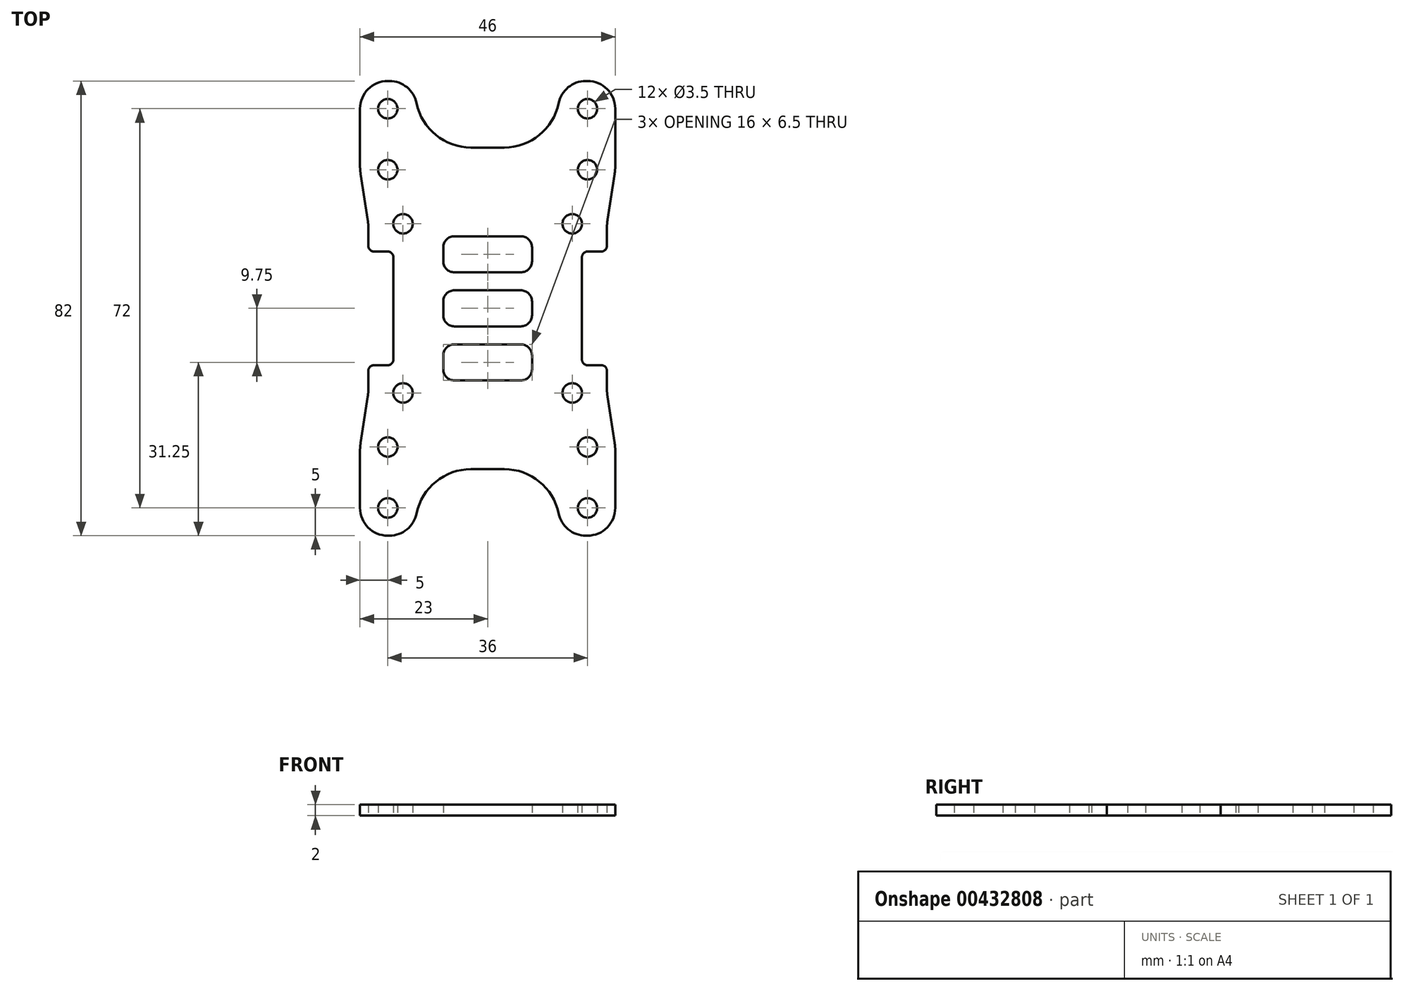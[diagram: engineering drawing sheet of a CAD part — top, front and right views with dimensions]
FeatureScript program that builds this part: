
annotation { "Feature Type Name" : "Feature", "Feature Type Description" : "" }
export const myFeature = defineFeature(function(context is Context, id is Id, definition is map)
    precondition{}
    {
        {
            var Q0;
            Q0=qCreatedBy(makeId("Top.planeOp"),FACE);
            var sketch = newSketch(context, id + "F0", { "sketchPlane" : qUnion([Q0])});
            skCircle(sketch, "E0", {"center": v(-18, 36) * mm, "radius": 1.75 * mm});
            skCircle(sketch, "E1", {"center": v(-18, 25) * mm, "radius": 1.75 * mm});
            skCircle(sketch, "E2", {"center": v(-15.25, 15.25) * mm, "radius": 1.75 * mm});
            skLineSegment(sketch, "E3", {"start": v(-18, 41) * mm, "end": v(-13, 41) * mm});
            skLineSegment(sketch, "E4", {"start": v(-23, 36) * mm, "end": v(-23, 25.76) * mm});
            skLineSegment(sketch, "E5", {"start": v(-21.5, 14.49) * mm, "end": v(-21.5, 11.25) * mm});
            skLineSegment(sketch, "E6", {"start": v(-22.88, 24.24) * mm, "end": v(-21.62, 16) * mm});
            skPoint(sketch, "E7.visualSharp", {"position": v(-23, 25) * mm});
            skArc(sketch, "E7.filletArc", {"start": v(-23, 25.76) * mm, "mid": v(-22.97, 25) * mm, "end": v(-22.88, 24.24) * mm});
            skPoint(sketch, "E8.visualSharp", {"position": v(-21.5, 15.25) * mm});
            skArc(sketch, "E8.filletArc", {"start": v(-21.5, 14.49) * mm, "mid": v(-21.53, 15.25) * mm, "end": v(-21.62, 16) * mm});
            skPoint(sketch, "E9.visualSharp", {"position": v(-23, 41) * mm});
            skArc(sketch, "E9.filletArc", {"start": v(-18, 41) * mm, "mid": v(-21.54, 39.54) * mm, "end": v(-23, 36) * mm});
            skArc(sketch, "E10.MirrorCS", {"start": v(23, 25.76) * mm, "mid": v(22.97, 25) * mm, "end": v(22.88, 24.24) * mm});
            skArc(sketch, "E11.MirrorCS", {"start": v(21.5, 14.49) * mm, "mid": v(21.53, 15.25) * mm, "end": v(21.62, 16) * mm});
            skCircle(sketch, "E12.MirrorC", {"center": v(18, 36) * mm, "radius": 1.75 * mm});
            skLineSegment(sketch, "E13.MirrorCS", {"start": v(21.5, 14.49) * mm, "end": v(21.5, 11.25) * mm});
            skLineSegment(sketch, "E14.MirrorCS", {"start": v(22.88, 24.24) * mm, "end": v(21.62, 16) * mm});
            skPoint(sketch, "E15.MirrorP", {"position": v(23, 25) * mm});
            skLineSegment(sketch, "E16.MirrorCS", {"start": v(23, 36) * mm, "end": v(23, 25.76) * mm});
            skLineSegment(sketch, "E17.MirrorCS", {"start": v(18, 41) * mm, "end": v(13, 41) * mm});
            skArc(sketch, "E18.MirrorCS", {"start": v(18, 41) * mm, "mid": v(21.54, 39.54) * mm, "end": v(23, 36) * mm});
            skPoint(sketch, "E19.MirrorP", {"position": v(21.5, 15.25) * mm});
            skCircle(sketch, "E20.MirrorC", {"center": v(15.25, 15.25) * mm, "radius": 1.75 * mm});
            skCircle(sketch, "E21.MirrorC", {"center": v(18, 25) * mm, "radius": 1.75 * mm});
            skPoint(sketch, "E22.MirrorP", {"position": v(23, 41) * mm});
            skArc(sketch, "E23.MirrorCS", {"start": v(-23, -25.76) * mm, "mid": v(-22.97, -25) * mm, "end": v(-22.88, -24.24) * mm});
            skArc(sketch, "E24.MirrorCS", {"start": v(-21.5, -14.49) * mm, "mid": v(-21.53, -15.25) * mm, "end": v(-21.62, -16) * mm});
            skArc(sketch, "E25.MirrorCS", {"start": v(23, -25.76) * mm, "mid": v(22.97, -25) * mm, "end": v(22.88, -24.24) * mm});
            skArc(sketch, "E26.MirrorCS", {"start": v(21.5, -14.49) * mm, "mid": v(21.53, -15.25) * mm, "end": v(21.62, -16) * mm});
            skCircle(sketch, "E27.MirrorC", {"center": v(-18, -36) * mm, "radius": 1.75 * mm});
            skLineSegment(sketch, "E28.MirrorCS", {"start": v(21.5, -14.49) * mm, "end": v(21.5, -11.25) * mm});
            skPoint(sketch, "E29.MirrorP", {"position": v(21.5, -15.25) * mm});
            skCircle(sketch, "E30.MirrorC", {"center": v(18, -25) * mm, "radius": 1.75 * mm});
            skArc(sketch, "E31.MirrorCS", {"start": v(18, -41) * mm, "mid": v(21.54, -39.54) * mm, "end": v(23, -36) * mm});
            skPoint(sketch, "E32.MirrorP", {"position": v(23, -25) * mm});
            skPoint(sketch, "E33.MirrorP", {"position": v(-21.5, -15.25) * mm});
            skCircle(sketch, "E34.MirrorC", {"center": v(-15.25, -15.25) * mm, "radius": 1.75 * mm});
            skLineSegment(sketch, "E35.MirrorCS", {"start": v(22.88, -24.24) * mm, "end": v(21.62, -16) * mm});
            skLineSegment(sketch, "E36.MirrorCS", {"start": v(23, -36) * mm, "end": v(23, -25.76) * mm});
            skPoint(sketch, "E37.MirrorP", {"position": v(-23, -41) * mm});
            skPoint(sketch, "E38.MirrorP", {"position": v(-23, -25) * mm});
            skPoint(sketch, "E39.MirrorP", {"position": v(23, -41) * mm});
            skLineSegment(sketch, "E40.MirrorCS", {"start": v(-18, -41) * mm, "end": v(-13, -41) * mm});
            skCircle(sketch, "E41.MirrorC", {"center": v(-18, -25) * mm, "radius": 1.75 * mm});
            skLineSegment(sketch, "E42.MirrorCS", {"start": v(-23, -36) * mm, "end": v(-23, -25.76) * mm});
            skLineSegment(sketch, "E43.MirrorCS", {"start": v(-21.5, -14.49) * mm, "end": v(-21.5, -11.25) * mm});
            skLineSegment(sketch, "E44.MirrorCS", {"start": v(-22.88, -24.24) * mm, "end": v(-21.62, -16) * mm});
            skArc(sketch, "E45.MirrorCS", {"start": v(-18, -41) * mm, "mid": v(-21.54, -39.54) * mm, "end": v(-23, -36) * mm});
            skCircle(sketch, "E46.MirrorC", {"center": v(18, -36) * mm, "radius": 1.75 * mm});
            skCircle(sketch, "E47.MirrorC", {"center": v(15.25, -15.25) * mm, "radius": 1.75 * mm});
            skLineSegment(sketch, "E48.MirrorCS", {"start": v(18, -41) * mm, "end": v(13, -41) * mm});
            skLineSegment(sketch, "E49", {"start": v(-13, 41) * mm, "end": v(-13, 39) * mm});
            skLineSegment(sketch, "E50", {"start": v(-3, 29) * mm, "end": v(0, 29) * mm});
            skPoint(sketch, "E51.visualSharp", {"position": v(-13, 29) * mm});
            skArc(sketch, "E51.filletArc", {"start": v(-13, 39) * mm, "mid": v(-10.07, 31.93) * mm, "end": v(-3, 29) * mm});
            skArc(sketch, "E52.MirrorCS", {"start": v(13, 39) * mm, "mid": v(10.07, 31.93) * mm, "end": v(3, 29) * mm});
            skLineSegment(sketch, "E53.MirrorCS", {"start": v(13, 41) * mm, "end": v(13, 39) * mm});
            skLineSegment(sketch, "E54.MirrorCS", {"start": v(3, 29) * mm, "end": v(0, 29) * mm});
            skLineSegment(sketch, "E55.MirrorCS", {"start": v(-13, -41) * mm, "end": v(-13, -39) * mm});
            skArc(sketch, "E56.MirrorCS", {"start": v(-13, -39) * mm, "mid": v(-10.07, -31.93) * mm, "end": v(-3, -29) * mm});
            skLineSegment(sketch, "E57.MirrorCS", {"start": v(-3, -29) * mm, "end": v(0, -29) * mm});
            skLineSegment(sketch, "E58.MirrorCS", {"start": v(3, -29) * mm, "end": v(0, -29) * mm});
            skArc(sketch, "E59.MirrorCS", {"start": v(13, -39) * mm, "mid": v(10.07, -31.93) * mm, "end": v(3, -29) * mm});
            skLineSegment(sketch, "E60.MirrorCS", {"start": v(13, -41) * mm, "end": v(13, -39) * mm});
            skPoint(sketch, "E61.orphan", {"position": v(0, 41) * mm});
            skPoint(sketch, "E62.orphan", {"position": v(0, -41) * mm});
            skLineSegment(sketch, "E63", {"start": v(-17, 9.25) * mm, "end": v(-17, -9.25) * mm});
            skLineSegment(sketch, "E64", {"start": v(-18, 10.25) * mm, "end": v(-20.5, 10.25) * mm});
            skLineSegment(sketch, "E65", {"start": v(-18, -10.25) * mm, "end": v(-20.5, -10.25) * mm});
            skPoint(sketch, "E66.orphan", {"position": v(-21.5, 0) * mm});
            skPoint(sketch, "E67.visualSharp", {"position": v(-17, 10.25) * mm});
            skArc(sketch, "E67.filletArc", {"start": v(-17, 9.25) * mm, "mid": v(-17.3, 9.96) * mm, "end": v(-18, 10.25) * mm});
            skPoint(sketch, "E68.visualSharp", {"position": v(-17, -10.25) * mm});
            skArc(sketch, "E68.filletArc", {"start": v(-18, -10.25) * mm, "mid": v(-17.3, -9.96) * mm, "end": v(-17, -9.25) * mm});
            skPoint(sketch, "E69.visualSharp", {"position": v(-21.5, 10.25) * mm});
            skArc(sketch, "E69.filletArc", {"start": v(-21.5, 11.25) * mm, "mid": v(-21.2, 10.54) * mm, "end": v(-20.5, 10.25) * mm});
            skPoint(sketch, "E70.visualSharp", {"position": v(-21.5, -10.25) * mm});
            skArc(sketch, "E70.filletArc", {"start": v(-20.5, -10.25) * mm, "mid": v(-21.2, -10.54) * mm, "end": v(-21.5, -11.25) * mm});
            skArc(sketch, "E71.MirrorCS", {"start": v(17, 9.25) * mm, "mid": v(17.3, 9.96) * mm, "end": v(18, 10.25) * mm});
            skLineSegment(sketch, "E72.MirrorCS", {"start": v(18, 10.25) * mm, "end": v(20.5, 10.25) * mm});
            skArc(sketch, "E73.MirrorCS", {"start": v(18, -10.25) * mm, "mid": v(17.3, -9.96) * mm, "end": v(17, -9.25) * mm});
            skLineSegment(sketch, "E74.MirrorCS", {"start": v(18, -10.25) * mm, "end": v(20.5, -10.25) * mm});
            skArc(sketch, "E75.MirrorCS", {"start": v(20.5, -10.25) * mm, "mid": v(21.2, -10.54) * mm, "end": v(21.5, -11.25) * mm});
            skArc(sketch, "E76.MirrorCS", {"start": v(21.5, 11.25) * mm, "mid": v(21.2, 10.54) * mm, "end": v(20.5, 10.25) * mm});
            skPoint(sketch, "E77.MirrorP", {"position": v(21.5, 0) * mm});
            skPoint(sketch, "E78.MirrorP", {"position": v(21.5, 10.25) * mm});
            skLineSegment(sketch, "E79.MirrorCS", {"start": v(17, 9.25) * mm, "end": v(17, -9.25) * mm});
            skPoint(sketch, "E80.MirrorP", {"position": v(17, 10.25) * mm});
            skPoint(sketch, "E81.MirrorP", {"position": v(17, -10.25) * mm});
            skPoint(sketch, "E82.MirrorP", {"position": v(21.5, -10.25) * mm});
            skLineSegment(sketch, "E83.bottom", {"start": v(-6, 13) * mm, "end": v(6, 13) * mm});
            skLineSegment(sketch, "E83.top", {"start": v(-6, -13) * mm, "end": v(6, -13) * mm});
            skLineSegment(sketch, "E83.left", {"start": v(-8, 11) * mm, "end": v(-8, 8.5) * mm});
            skLineSegment(sketch, "E83.right", {"start": v(8, 11) * mm, "end": v(8, 8.5) * mm});
            skPoint(sketch, "E83.middle", {"position": v(0, 0) * mm});
            skLineSegment(sketch, "E84", {"start": v(-6, 6.5) * mm, "end": v(6, 6.5) * mm});
            skLineSegment(sketch, "E85", {"start": v(-6, 3.25) * mm, "end": v(6, 3.25) * mm});
            skLineSegment(sketch, "E86.MirrorCS", {"start": v(-6, -3.25) * mm, "end": v(6, -3.25) * mm});
            skLineSegment(sketch, "E87.MirrorCS", {"start": v(-6, -6.5) * mm, "end": v(6, -6.5) * mm});
            skLineSegment(sketch, "E88.trimOffspring", {"start": v(8, 1.25) * mm, "end": v(8, -1.25) * mm});
            skLineSegment(sketch, "E89.trimOffspring", {"start": v(-8, 1.25) * mm, "end": v(-8, -1.25) * mm});
            skLineSegment(sketch, "E90.trimOffspring", {"start": v(-8, -8.5) * mm, "end": v(-8, -11) * mm});
            skLineSegment(sketch, "E91.trimOffspring", {"start": v(8, -8.5) * mm, "end": v(8, -11) * mm});
            skPoint(sketch, "E92.visualSharp", {"position": v(-8, 6.5) * mm});
            skArc(sketch, "E92.filletArc", {"start": v(-8, 8.5) * mm, "mid": v(-7.41, 7.09) * mm, "end": v(-6, 6.5) * mm});
            skPoint(sketch, "E93.visualSharp", {"position": v(-8, 13) * mm});
            skArc(sketch, "E93.filletArc", {"start": v(-6, 13) * mm, "mid": v(-7.41, 12.41) * mm, "end": v(-8, 11) * mm});
            skPoint(sketch, "E94.visualSharp", {"position": v(8, 13) * mm});
            skArc(sketch, "E94.filletArc", {"start": v(8, 11) * mm, "mid": v(7.41, 12.41) * mm, "end": v(6, 13) * mm});
            skPoint(sketch, "E95.visualSharp", {"position": v(8, 3.25) * mm});
            skArc(sketch, "E95.filletArc", {"start": v(8, 1.25) * mm, "mid": v(7.41, 2.66) * mm, "end": v(6, 3.25) * mm});
            skPoint(sketch, "E96.visualSharp", {"position": v(8, -3.25) * mm});
            skArc(sketch, "E96.filletArc", {"start": v(6, -3.25) * mm, "mid": v(7.41, -2.66) * mm, "end": v(8, -1.25) * mm});
            skPoint(sketch, "E97.visualSharp", {"position": v(-8, -3.25) * mm});
            skArc(sketch, "E97.filletArc", {"start": v(-8, -1.25) * mm, "mid": v(-7.41, -2.66) * mm, "end": v(-6, -3.25) * mm});
            skPoint(sketch, "E98.visualSharp", {"position": v(-8, 3.25) * mm});
            skArc(sketch, "E98.filletArc", {"start": v(-6, 3.25) * mm, "mid": v(-7.41, 2.66) * mm, "end": v(-8, 1.25) * mm});
            skPoint(sketch, "E99.visualSharp", {"position": v(-8, -6.5) * mm});
            skArc(sketch, "E99.filletArc", {"start": v(-6, -6.5) * mm, "mid": v(-7.41, -7.09) * mm, "end": v(-8, -8.5) * mm});
            skPoint(sketch, "E100.visualSharp", {"position": v(-8, -13) * mm});
            skArc(sketch, "E100.filletArc", {"start": v(-8, -11) * mm, "mid": v(-7.41, -12.41) * mm, "end": v(-6, -13) * mm});
            skPoint(sketch, "E101.visualSharp", {"position": v(8, -6.5) * mm});
            skArc(sketch, "E101.filletArc", {"start": v(8, -8.5) * mm, "mid": v(7.41, -7.09) * mm, "end": v(6, -6.5) * mm});
            skPoint(sketch, "E102.visualSharp", {"position": v(8, -13) * mm});
            skArc(sketch, "E102.filletArc", {"start": v(6, -13) * mm, "mid": v(7.41, -12.41) * mm, "end": v(8, -11) * mm});
            skPoint(sketch, "E103.visualSharp", {"position": v(8, 6.5) * mm});
            skArc(sketch, "E103.filletArc", {"start": v(6, 6.5) * mm, "mid": v(7.41, 7.09) * mm, "end": v(8, 8.5) * mm});
            skSolve(sketch);
        }
        {
            var Q0;
            Q0=makeQuery(id+"F0.imprint","IMPRINT",FACE,{"disambiguationData":[TD([[makeQuery(id+"F0.imprint","IMPRINT",EDGE,{"derivedFrom":sQuery(id+"F0.wireOp",EDGE,"E0")}),-1.0]])]});
            extrude(context, id + "F1", {"entities" : qUnion([Q0]), "depth" : 2 * mm});
        }
        {
            var Q0;
            Q0=makeQuery(id+"F1.opExtrude","SWEPT_EDGE",EDGE,{"disambiguationData":[OSD([sQuery(id+"F0.wireOp",EDGE,"E40.MirrorCS"),sQuery(id+"F0.wireOp",EDGE,"E55.MirrorCS")])]});
            var Q1;
            Q1=makeQuery(id+"F1.opExtrude","SWEPT_EDGE",EDGE,{"disambiguationData":[OSD([sQuery(id+"F0.wireOp",EDGE,"E48.MirrorCS"),sQuery(id+"F0.wireOp",EDGE,"E60.MirrorCS")])]});
            var Q2;
            Q2=makeQuery(id+"F1.opExtrude","SWEPT_EDGE",EDGE,{"disambiguationData":[OSD([sQuery(id+"F0.wireOp",EDGE,"E3"),sQuery(id+"F0.wireOp",EDGE,"E49")])]});
            var Q3;
            Q3=makeQuery(id+"F1.opExtrude","SWEPT_EDGE",EDGE,{"disambiguationData":[OSD([sQuery(id+"F0.wireOp",EDGE,"E17.MirrorCS"),sQuery(id+"F0.wireOp",EDGE,"E53.MirrorCS")])]});
            fillet(context, id + "F2", {"entities" : qUnion([Q0, Q1, Q2, Q3]), "radius" : 5 * mm, "tangentPropagation" : true, "allowEdgeOverflow" : false});
        }
    });
